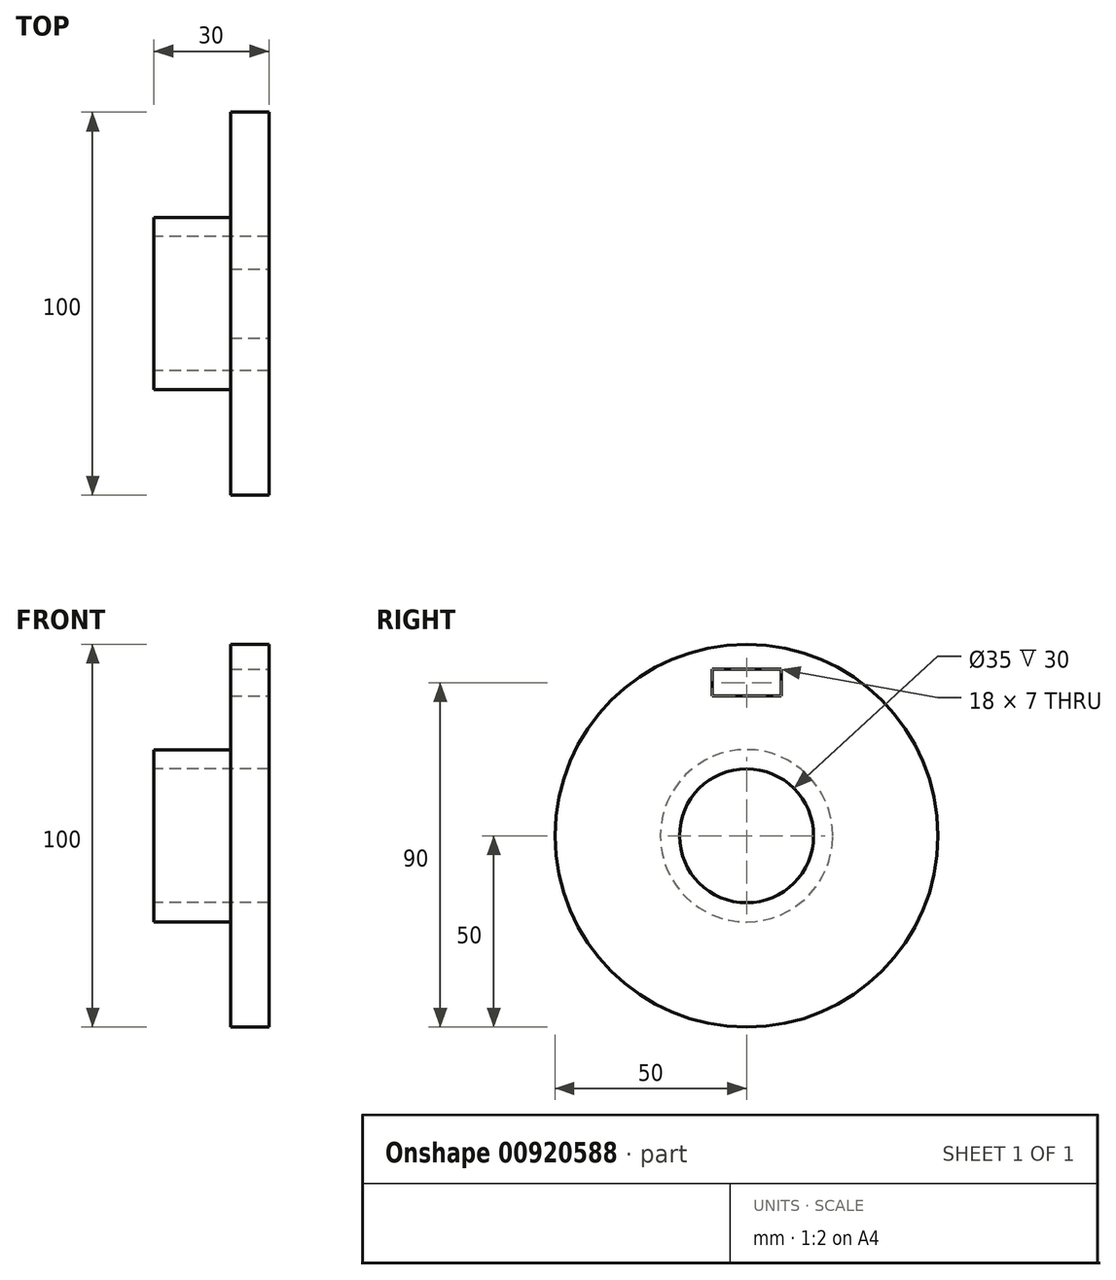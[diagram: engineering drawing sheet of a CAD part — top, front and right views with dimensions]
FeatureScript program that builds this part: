
annotation { "Feature Type Name" : "Feature", "Feature Type Description" : "" }
export const myFeature = defineFeature(function(context is Context, id is Id, definition is map)
    precondition{}
    {
        {
            var Q0;
            Q0=qCreatedBy(makeId("Front.planeOp"),FACE);
            var sketch = newSketch(context, id + "F0", { "sketchPlane" : qUnion([Q0])});
            skLineSegment(sketch, "E0", {"start": v(0, 0) * mm, "end": v(47.38, 0) * mm, "construction": true});
            skLineSegment(sketch, "E1", {"start": v(0, 50) * mm, "end": v(0, 17.5) * mm});
            skLineSegment(sketch, "E2", {"start": v(0, 17.5) * mm, "end": v(-30, 17.5) * mm});
            skLineSegment(sketch, "E3", {"start": v(-30, 17.5) * mm, "end": v(-30, 22.5) * mm});
            skLineSegment(sketch, "E4", {"start": v(-30, 22.5) * mm, "end": v(-10, 22.5) * mm});
            skLineSegment(sketch, "E5", {"start": v(-10, 22.5) * mm, "end": v(-10, 50) * mm});
            skLineSegment(sketch, "E6", {"start": v(0, 50) * mm, "end": v(-10, 50) * mm});
            skSolve(sketch);
        }
        {
            var Q0;
            Q0=makeQuery(id+"F0.imprint","IMPRINT",FACE,{"disambiguationData":[TD([[makeQuery(id+"F0.imprint","IMPRINT",EDGE,{"derivedFrom":sQuery(id+"F0.wireOp",EDGE,"E1")}),-1.0]])]});
            var Q1;
            Q1=sQuery(id+"F0.wireOp",EDGE,"E0");
            revolve(context, id + "F1", {"surfaceOperationType" : NewSurfaceOperationType.NEW, "entities" : qUnion([Q0]), "axis" : qUnion([Q1]), "revolveType" : RevolveType.FULL});
        }
        {
            var Q0;
            Q0=makeQuery(id+"F1.opRevolve","SWEPT_FACE",FACE,{"disambiguationData":[OSD([sQuery(id+"F0.wireOp",EDGE,"E1")])]});
            var sketch = newSketch(context, id + "F2", { "sketchPlane" : qUnion([Q0])});
            skLineSegment(sketch, "E7.bottom", {"start": v(-9, 43.5) * mm, "end": v(9, 43.5) * mm});
            skLineSegment(sketch, "E7.top", {"start": v(-9, 36.5) * mm, "end": v(9, 36.5) * mm});
            skLineSegment(sketch, "E7.left", {"start": v(-9, 43.5) * mm, "end": v(-9, 36.5) * mm});
            skLineSegment(sketch, "E7.right", {"start": v(9, 43.5) * mm, "end": v(9, 36.5) * mm});
            skLineSegment(sketch, "E8", {"start": v(-9, 40) * mm, "end": v(9, 40) * mm, "construction": true});
            skSolve(sketch);
        }
        {
            var Q0;
            Q0=makeQuery(id+"F2.imprint","IMPRINT",FACE,{"disambiguationData":[TD([[makeQuery(id+"F2.imprint","IMPRINT",EDGE,{"derivedFrom":sQuery(id+"F2.wireOp",EDGE,"E7.bottom")}),-1.0]])]});
            extrude(context, id + "F3", {"entities" : qUnion([Q0]), "operationType" : NewBodyOperationType.REMOVE, "endBound" : BoundingType.THROUGH_ALL, "oppositeDirection" : true, "depth" : 25 * mm, "offsetDistance" : 25 * mm});
        }
    });
